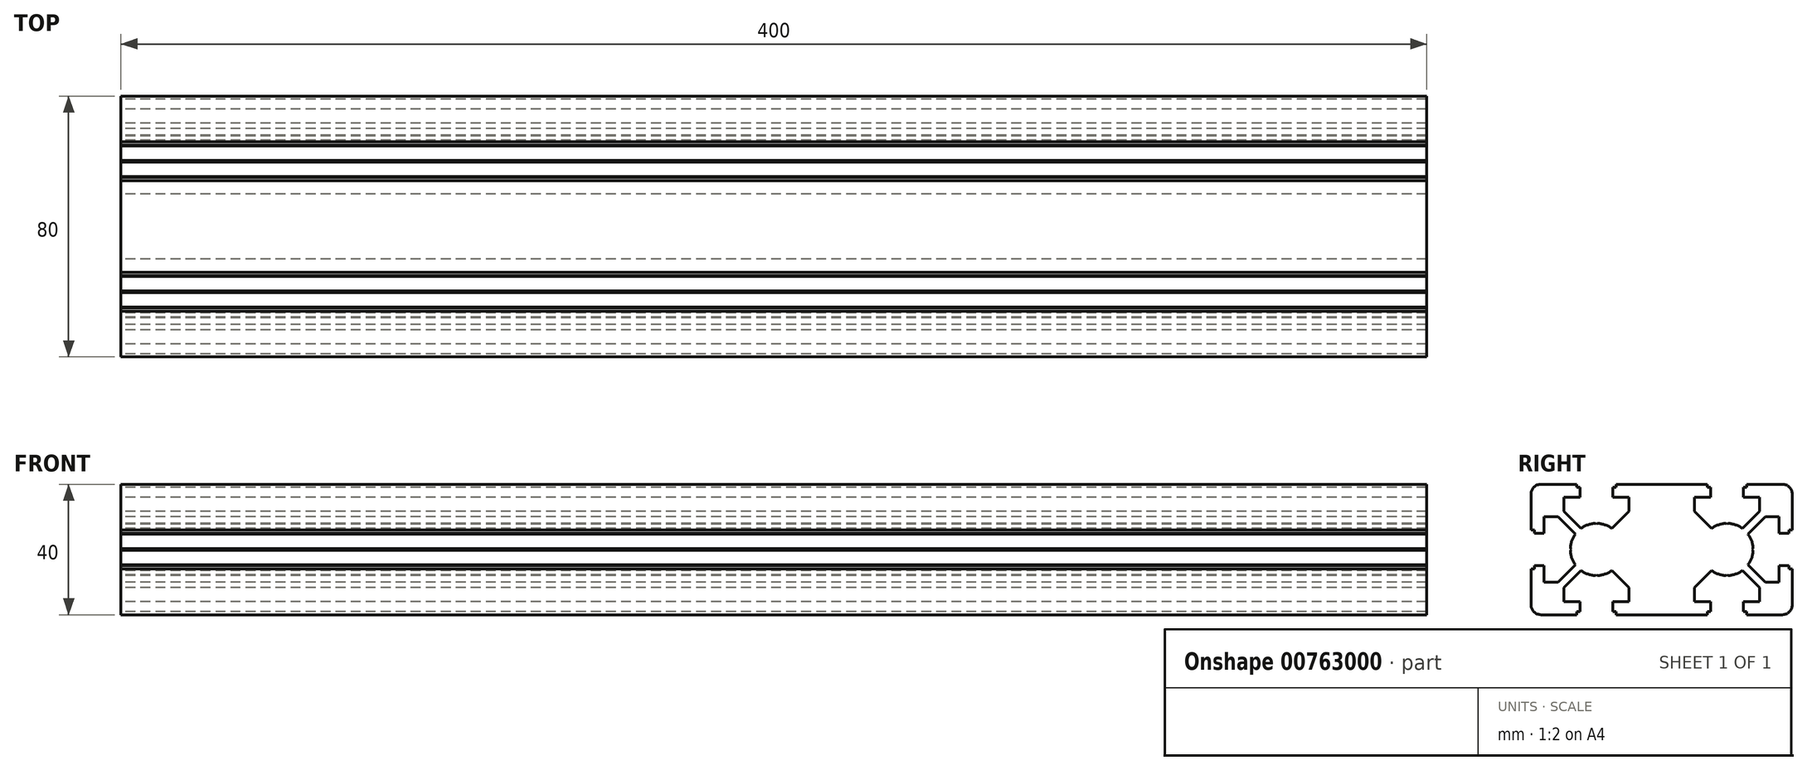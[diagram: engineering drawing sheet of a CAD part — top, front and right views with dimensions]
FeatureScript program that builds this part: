
annotation { "Feature Type Name" : "Feature", "Feature Type Description" : "" }
export const myFeature = defineFeature(function(context is Context, id is Id, definition is map)
    precondition{}
    {
        {
            var Q0;
            Q0=qCreatedBy(makeId("Right.planeOp"),FACE);
            var sketch = newSketch(context, id + "F0", { "sketchPlane" : qUnion([Q0])});
            skLineSegment(sketch, "E0.0.0", {"start": v(14.82, -7.7) * mm, "end": v(13.82, -7.7) * mm});
            skLineSegment(sketch, "E0.0.1", {"start": v(13.82, -7.7) * mm, "end": v(13.82, -6.7) * mm});
            skLineSegment(sketch, "E0.0.2", {"start": v(13.82, -6.7) * mm, "end": v(10.82, -6.7) * mm});
            skLineSegment(sketch, "E0.0.3", {"start": v(10.82, -6.7) * mm, "end": v(10.82, -11.7) * mm});
            skLineSegment(sketch, "E0.0.4", {"start": v(10.82, -11.7) * mm, "end": v(6.51, -11.7) * mm});
            skLineSegment(sketch, "E0.0.5", {"start": v(6.51, -11.7) * mm, "end": v(1.26, -6.45) * mm});
            skArc(sketch, "E0.0.6", {"start": v(1.26, -6.45) * mm, "mid": v(2.37, -4.35) * mm, "end": v(2.81, -2.02) * mm});
            skLineSegment(sketch, "E0.0.7", {"start": v(2.81, -2.02) * mm, "end": v(2.52, -1.7) * mm});
            skLineSegment(sketch, "E0.0.8", {"start": v(2.52, -1.7) * mm, "end": v(2.81, -1.4) * mm});
            skArc(sketch, "E0.0.9", {"start": v(2.81, -1.4) * mm, "mid": v(2.37, 0.93) * mm, "end": v(1.26, 3.04) * mm});
            skLineSegment(sketch, "E0.0.10", {"start": v(1.26, 3.04) * mm, "end": v(6.51, 8.3) * mm});
            skLineSegment(sketch, "E0.0.11", {"start": v(6.51, 8.3) * mm, "end": v(10.82, 8.3) * mm});
            skLineSegment(sketch, "E0.0.12", {"start": v(10.82, 8.3) * mm, "end": v(10.82, 3.3) * mm});
            skLineSegment(sketch, "E0.0.13", {"start": v(10.82, 3.3) * mm, "end": v(13.82, 3.3) * mm});
            skLineSegment(sketch, "E0.0.14", {"start": v(13.82, 3.3) * mm, "end": v(13.82, 4.3) * mm});
            skLineSegment(sketch, "E0.0.15", {"start": v(13.82, 4.3) * mm, "end": v(14.82, 4.3) * mm});
            skLineSegment(sketch, "E0.0.16", {"start": v(14.82, 4.3) * mm, "end": v(14.82, 15.3) * mm});
            skArc(sketch, "E0.0.17", {"start": v(14.82, 15.3) * mm, "mid": v(13.94, 17.41) * mm, "end": v(11.82, 18.3) * mm});
            skLineSegment(sketch, "E0.0.18", {"start": v(11.82, 18.3) * mm, "end": v(0.82, 18.3) * mm});
            skLineSegment(sketch, "E0.0.19", {"start": v(0.82, 18.3) * mm, "end": v(0.82, 17.3) * mm});
            skLineSegment(sketch, "E0.0.20", {"start": v(0.82, 17.3) * mm, "end": v(-0.18, 17.3) * mm});
            skLineSegment(sketch, "E0.0.21", {"start": v(-0.18, 17.3) * mm, "end": v(-0.18, 14.3) * mm});
            skLineSegment(sketch, "E0.0.22", {"start": v(-0.18, 14.3) * mm, "end": v(4.82, 14.3) * mm});
            skLineSegment(sketch, "E0.0.23", {"start": v(4.82, 14.3) * mm, "end": v(4.82, 9.99) * mm});
            skLineSegment(sketch, "E0.0.24", {"start": v(4.82, 9.99) * mm, "end": v(-0.44, 4.73) * mm});
            skArc(sketch, "E0.0.25", {"start": v(-0.44, 4.73) * mm, "mid": v(-2.54, 5.84) * mm, "end": v(-4.88, 6.29) * mm});
            skLineSegment(sketch, "E0.0.26", {"start": v(-4.88, 6.29) * mm, "end": v(-5.18, 6) * mm});
            skLineSegment(sketch, "E0.0.27", {"start": v(-5.18, 6) * mm, "end": v(-5.49, 6.29) * mm});
            skArc(sketch, "E0.0.28", {"start": v(-5.49, 6.29) * mm, "mid": v(-7.83, 5.84) * mm, "end": v(-9.93, 4.73) * mm});
            skLineSegment(sketch, "E0.0.29", {"start": v(-9.93, 4.73) * mm, "end": v(-15.18, 9.99) * mm});
            skLineSegment(sketch, "E0.0.30", {"start": v(-15.18, 9.99) * mm, "end": v(-15.18, 14.3) * mm});
            skLineSegment(sketch, "E0.0.31", {"start": v(-15.18, 14.3) * mm, "end": v(-10.18, 14.3) * mm});
            skLineSegment(sketch, "E0.0.32", {"start": v(-10.18, 14.3) * mm, "end": v(-10.18, 17.3) * mm});
            skLineSegment(sketch, "E0.0.33", {"start": v(-10.18, 17.3) * mm, "end": v(-11.18, 17.3) * mm});
            skLineSegment(sketch, "E0.0.34", {"start": v(-11.18, 17.3) * mm, "end": v(-11.18, 18.3) * mm});
            skLineSegment(sketch, "E0.0.35", {"start": v(-11.18, 18.3) * mm, "end": v(-39.18, 18.3) * mm});
            skLineSegment(sketch, "E0.0.36", {"start": v(-39.18, 18.3) * mm, "end": v(-39.18, 17.3) * mm});
            skLineSegment(sketch, "E0.0.37", {"start": v(-39.18, 17.3) * mm, "end": v(-40.18, 17.3) * mm});
            skLineSegment(sketch, "E0.0.38", {"start": v(-40.18, 17.3) * mm, "end": v(-40.18, 14.3) * mm});
            skLineSegment(sketch, "E0.0.39", {"start": v(-40.18, 14.3) * mm, "end": v(-35.18, 14.3) * mm});
            skLineSegment(sketch, "E0.0.40", {"start": v(-35.18, 14.3) * mm, "end": v(-35.18, 9.99) * mm});
            skLineSegment(sketch, "E0.0.41", {"start": v(-35.18, 9.99) * mm, "end": v(-40.44, 4.73) * mm});
            skArc(sketch, "E0.0.42", {"start": v(-40.44, 4.73) * mm, "mid": v(-42.54, 5.84) * mm, "end": v(-44.88, 6.29) * mm});
            skLineSegment(sketch, "E0.0.43", {"start": v(-44.88, 6.29) * mm, "end": v(-45.18, 6) * mm});
            skLineSegment(sketch, "E0.0.44", {"start": v(-45.18, 6) * mm, "end": v(-45.49, 6.29) * mm});
            skArc(sketch, "E0.0.45", {"start": v(-45.49, 6.29) * mm, "mid": v(-47.83, 5.84) * mm, "end": v(-49.93, 4.73) * mm});
            skLineSegment(sketch, "E0.0.46", {"start": v(-49.93, 4.73) * mm, "end": v(-55.18, 9.99) * mm});
            skLineSegment(sketch, "E0.0.47", {"start": v(-55.18, 9.99) * mm, "end": v(-55.18, 14.3) * mm});
            skLineSegment(sketch, "E0.0.48", {"start": v(-55.18, 14.3) * mm, "end": v(-50.18, 14.3) * mm});
            skLineSegment(sketch, "E0.0.49", {"start": v(-50.18, 14.3) * mm, "end": v(-50.18, 17.3) * mm});
            skLineSegment(sketch, "E0.0.50", {"start": v(-50.18, 17.3) * mm, "end": v(-51.18, 17.3) * mm});
            skLineSegment(sketch, "E0.0.51", {"start": v(-51.18, 17.3) * mm, "end": v(-51.18, 18.3) * mm});
            skLineSegment(sketch, "E0.0.52", {"start": v(-51.18, 18.3) * mm, "end": v(-62.18, 18.3) * mm});
            skArc(sketch, "E0.0.53", {"start": v(-62.18, 18.3) * mm, "mid": v(-64.3, 17.41) * mm, "end": v(-65.18, 15.3) * mm});
            skLineSegment(sketch, "E0.0.54", {"start": v(-65.18, 15.3) * mm, "end": v(-65.18, 4.3) * mm});
            skLineSegment(sketch, "E0.0.55", {"start": v(-65.18, 4.3) * mm, "end": v(-64.18, 4.3) * mm});
            skLineSegment(sketch, "E0.0.56", {"start": v(-64.18, 4.3) * mm, "end": v(-64.18, 3.3) * mm});
            skLineSegment(sketch, "E0.0.57", {"start": v(-64.18, 3.3) * mm, "end": v(-61.18, 3.3) * mm});
            skLineSegment(sketch, "E0.0.58", {"start": v(-61.18, 3.3) * mm, "end": v(-61.18, 8.3) * mm});
            skLineSegment(sketch, "E0.0.59", {"start": v(-61.18, 8.3) * mm, "end": v(-56.88, 8.3) * mm});
            skLineSegment(sketch, "E0.0.60", {"start": v(-56.88, 8.3) * mm, "end": v(-51.62, 3.04) * mm});
            skArc(sketch, "E0.0.61", {"start": v(-51.62, 3.04) * mm, "mid": v(-52.73, 0.93) * mm, "end": v(-53.18, -1.4) * mm});
            skLineSegment(sketch, "E0.0.62", {"start": v(-53.18, -1.4) * mm, "end": v(-52.88, -1.7) * mm});
            skLineSegment(sketch, "E0.0.63", {"start": v(-52.88, -1.7) * mm, "end": v(-53.18, -2.02) * mm});
            skArc(sketch, "E0.0.64", {"start": v(-53.18, -2.02) * mm, "mid": v(-52.73, -4.35) * mm, "end": v(-51.62, -6.45) * mm});
            skLineSegment(sketch, "E0.0.65", {"start": v(-51.62, -6.45) * mm, "end": v(-56.88, -11.7) * mm});
            skLineSegment(sketch, "E0.0.66", {"start": v(-56.88, -11.7) * mm, "end": v(-61.18, -11.7) * mm});
            skLineSegment(sketch, "E0.0.67", {"start": v(-61.18, -11.7) * mm, "end": v(-61.18, -6.7) * mm});
            skLineSegment(sketch, "E0.0.68", {"start": v(-61.18, -6.7) * mm, "end": v(-64.18, -6.7) * mm});
            skLineSegment(sketch, "E0.0.69", {"start": v(-64.18, -6.7) * mm, "end": v(-64.18, -7.7) * mm});
            skLineSegment(sketch, "E0.0.70", {"start": v(-64.18, -7.7) * mm, "end": v(-65.18, -7.7) * mm});
            skLineSegment(sketch, "E0.0.71", {"start": v(-65.18, -7.7) * mm, "end": v(-65.18, -18.7) * mm});
            skArc(sketch, "E0.0.72", {"start": v(-65.18, -18.7) * mm, "mid": v(-64.3, -20.83) * mm, "end": v(-62.18, -21.7) * mm});
            skLineSegment(sketch, "E0.0.73", {"start": v(-62.18, -21.7) * mm, "end": v(-51.18, -21.7) * mm});
            skLineSegment(sketch, "E0.0.74", {"start": v(-51.18, -21.7) * mm, "end": v(-51.18, -20.7) * mm});
            skLineSegment(sketch, "E0.0.75", {"start": v(-51.18, -20.7) * mm, "end": v(-50.18, -20.7) * mm});
            skLineSegment(sketch, "E0.0.76", {"start": v(-50.18, -20.7) * mm, "end": v(-50.18, -17.7) * mm});
            skLineSegment(sketch, "E0.0.77", {"start": v(-50.18, -17.7) * mm, "end": v(-55.18, -17.7) * mm});
            skLineSegment(sketch, "E0.0.78", {"start": v(-55.18, -17.7) * mm, "end": v(-55.18, -13.4) * mm});
            skLineSegment(sketch, "E0.0.79", {"start": v(-55.18, -13.4) * mm, "end": v(-49.93, -8.15) * mm});
            skArc(sketch, "E0.0.80", {"start": v(-49.93, -8.15) * mm, "mid": v(-47.83, -9.26) * mm, "end": v(-45.49, -9.7) * mm});
            skLineSegment(sketch, "E0.0.81", {"start": v(-45.49, -9.7) * mm, "end": v(-45.18, -9.4) * mm});
            skLineSegment(sketch, "E0.0.82", {"start": v(-45.18, -9.4) * mm, "end": v(-44.88, -9.7) * mm});
            skArc(sketch, "E0.0.83", {"start": v(-44.88, -9.7) * mm, "mid": v(-42.54, -9.26) * mm, "end": v(-40.44, -8.15) * mm});
            skLineSegment(sketch, "E0.0.84", {"start": v(-40.44, -8.15) * mm, "end": v(-35.18, -13.4) * mm});
            skLineSegment(sketch, "E0.0.85", {"start": v(-35.18, -13.4) * mm, "end": v(-35.18, -17.7) * mm});
            skLineSegment(sketch, "E0.0.86", {"start": v(-35.18, -17.7) * mm, "end": v(-40.18, -17.7) * mm});
            skLineSegment(sketch, "E0.0.87", {"start": v(-40.18, -17.7) * mm, "end": v(-40.18, -20.7) * mm});
            skLineSegment(sketch, "E0.0.88", {"start": v(-40.18, -20.7) * mm, "end": v(-39.18, -20.7) * mm});
            skLineSegment(sketch, "E0.0.89", {"start": v(-39.18, -20.7) * mm, "end": v(-39.18, -21.7) * mm});
            skLineSegment(sketch, "E0.0.90", {"start": v(-39.18, -21.7) * mm, "end": v(-11.18, -21.7) * mm});
            skLineSegment(sketch, "E0.0.91", {"start": v(-11.18, -21.7) * mm, "end": v(-11.18, -20.7) * mm});
            skLineSegment(sketch, "E0.0.92", {"start": v(-11.18, -20.7) * mm, "end": v(-10.18, -20.7) * mm});
            skLineSegment(sketch, "E0.0.93", {"start": v(-10.18, -20.7) * mm, "end": v(-10.18, -17.7) * mm});
            skLineSegment(sketch, "E0.0.94", {"start": v(-10.18, -17.7) * mm, "end": v(-15.18, -17.7) * mm});
            skLineSegment(sketch, "E0.0.95", {"start": v(-15.18, -17.7) * mm, "end": v(-15.18, -13.4) * mm});
            skLineSegment(sketch, "E0.0.96", {"start": v(-15.18, -13.4) * mm, "end": v(-9.93, -8.15) * mm});
            skArc(sketch, "E0.0.97", {"start": v(-9.93, -8.15) * mm, "mid": v(-7.83, -9.26) * mm, "end": v(-5.49, -9.7) * mm});
            skLineSegment(sketch, "E0.0.98", {"start": v(-5.49, -9.7) * mm, "end": v(-5.18, -9.4) * mm});
            skLineSegment(sketch, "E0.0.99", {"start": v(-5.18, -9.4) * mm, "end": v(-4.88, -9.7) * mm});
            skArc(sketch, "E0.0.100", {"start": v(-4.88, -9.7) * mm, "mid": v(-2.54, -9.26) * mm, "end": v(-0.44, -8.15) * mm});
            skLineSegment(sketch, "E0.0.101", {"start": v(-0.44, -8.15) * mm, "end": v(4.82, -13.4) * mm});
            skLineSegment(sketch, "E0.0.102", {"start": v(4.82, -13.4) * mm, "end": v(4.82, -17.7) * mm});
            skLineSegment(sketch, "E0.0.103", {"start": v(4.82, -17.7) * mm, "end": v(-0.18, -17.7) * mm});
            skLineSegment(sketch, "E0.0.104", {"start": v(-0.18, -17.7) * mm, "end": v(-0.18, -20.7) * mm});
            skLineSegment(sketch, "E0.0.105", {"start": v(-0.18, -20.7) * mm, "end": v(0.82, -20.7) * mm});
            skLineSegment(sketch, "E0.0.106", {"start": v(0.82, -20.7) * mm, "end": v(0.82, -21.7) * mm});
            skLineSegment(sketch, "E0.0.107", {"start": v(0.82, -21.7) * mm, "end": v(11.82, -21.7) * mm});
            skArc(sketch, "E0.0.108", {"start": v(11.82, -21.7) * mm, "mid": v(13.94, -20.83) * mm, "end": v(14.82, -18.7) * mm});
            skLineSegment(sketch, "E0.0.109", {"start": v(14.82, -18.7) * mm, "end": v(14.82, -7.7) * mm});
            skSolve(sketch);
        }
        {
            var Q0;
            Q0=makeQuery(id+"F0.imprint","IMPRINT",FACE,{"disambiguationData":[TD([[makeQuery(id+"F0.imprint","IMPRINT",EDGE,{"derivedFrom":sQuery(id+"F0.wireOp",EDGE,"E0.0.0")}),1.0]])]});
            extrude(context, id + "F1", {"entities" : qUnion([Q0]), "endBound" : BoundingType.SYMMETRIC, "depth" : 400 * mm, "offsetDistance" : 25 * mm});
        }
    });
